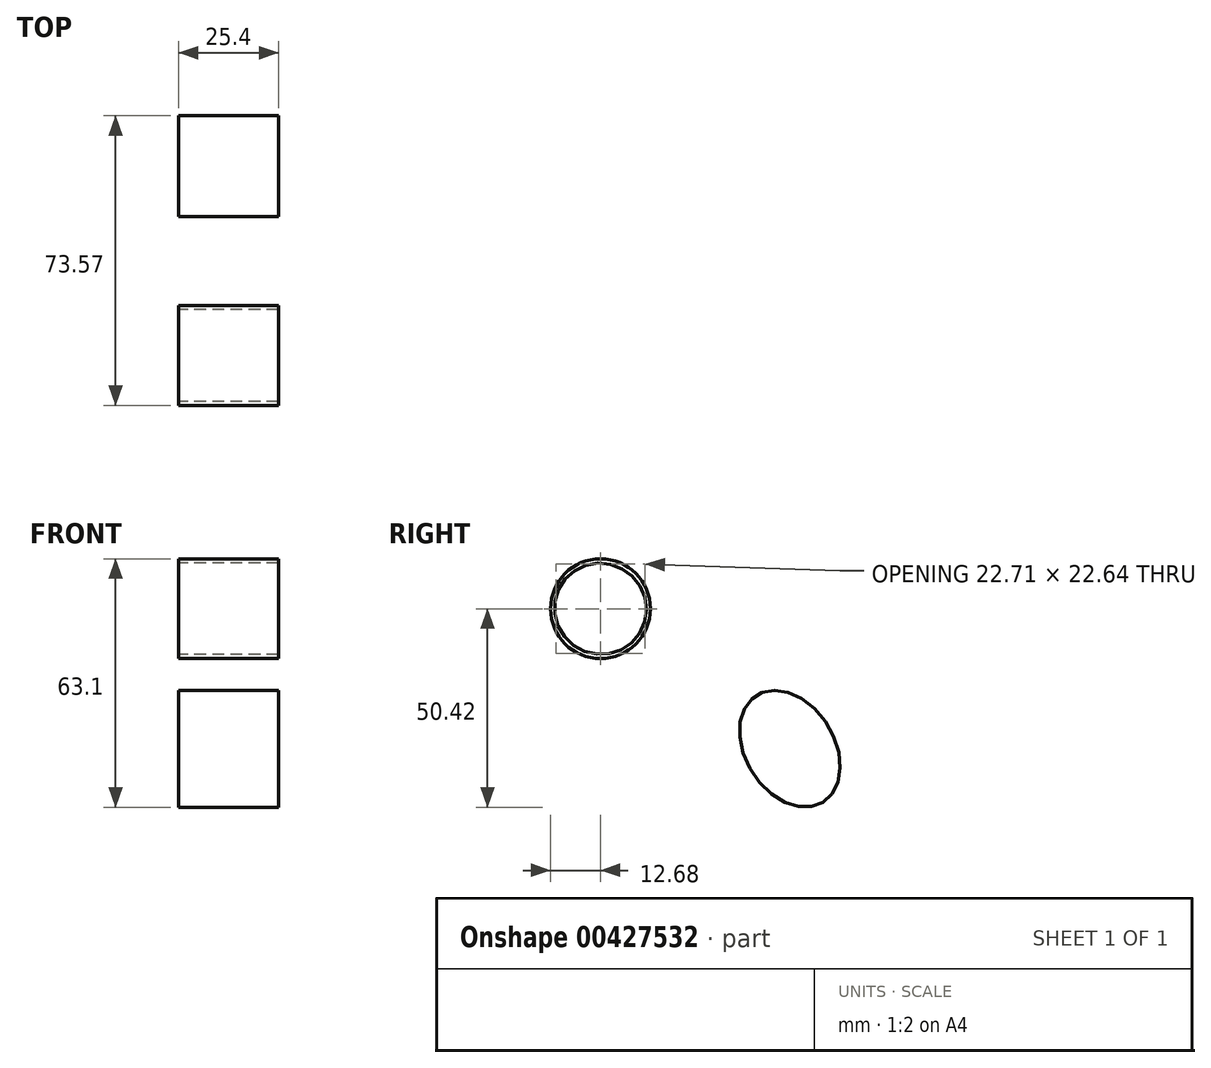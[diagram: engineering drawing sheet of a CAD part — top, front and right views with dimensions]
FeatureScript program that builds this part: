
annotation { "Feature Type Name" : "Feature", "Feature Type Description" : "" }
export const myFeature = defineFeature(function(context is Context, id is Id, definition is map)
    precondition{}
    {
        {
            var Q0;
            Q0=qCreatedBy(makeId("Right.planeOp"),FACE);
            var sketch = newSketch(context, id + "F0", { "sketchPlane" : qUnion([Q0])});
            skCircle(sketch, "E0", {"center": v(0, 0) * mm, "radius": 12.68 * mm});
            skEllipse(sketch, "E1", {"center": v(0, 0) * mm, "majorRadius": 11.53 * mm, "minorRadius": 11.7 * mm, "majorAxis": v(-0.54, -0.84)});
            skEllipse(sketch, "E2", {"center": v(48.1, -35.56) * mm, "majorRadius": 16 * mm, "minorRadius": 11.32 * mm, "majorAxis": v(0.53, -0.85)});
            skSolve(sketch);
        }
        {
            var Q0;
            Q0 = qSketchRegion(id + "F0", true);
            extrude(context, id + "F1", {"entities" : qUnion([Q0]), "depth" : 25.4 * mm});
        }
    });
